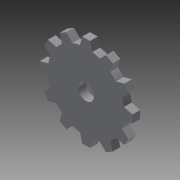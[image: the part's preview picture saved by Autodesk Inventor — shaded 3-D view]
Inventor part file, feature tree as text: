
AUTODESK INVENTOR PART (.ipt)
format: ipt  version: 2013 (Build 170138000, 138)  size: 143,872 bytes
history: native  units: in
note: dims shown in document units (in); Inventor stores cm internally (conversion verified against a paired STEP export)
features: extrude x2, sketch x2
ambient origin geometry x8: Origin, YZ Plane, XZ Plane, XY Plane, X Axis, Y Axis, Z Axis, Center Point
bodies: Solid1 (feature_tree)
feature tree (4):
  extrude  "Extrusion1"  Depth=0.0625in
  extrude  "Extrusion2"  TaperAngle=120.0deg  [1 undecoded]
  sketch  "Sketch2"  dims[d1=4.7244in d3=360.0deg d5=0.0625in]
  sketch  "Sketch3"  dims[d6=0.375in d7=120.0deg d8=0.0625in d9=0.0in d10=0.125in d11=0.125in d12=0.0in]
note: 1 required parameter value undecoded (feature->parameter linkage not recoverable at this tier; creation-order binding heuristic only, values carry confidence <= 0.55)
